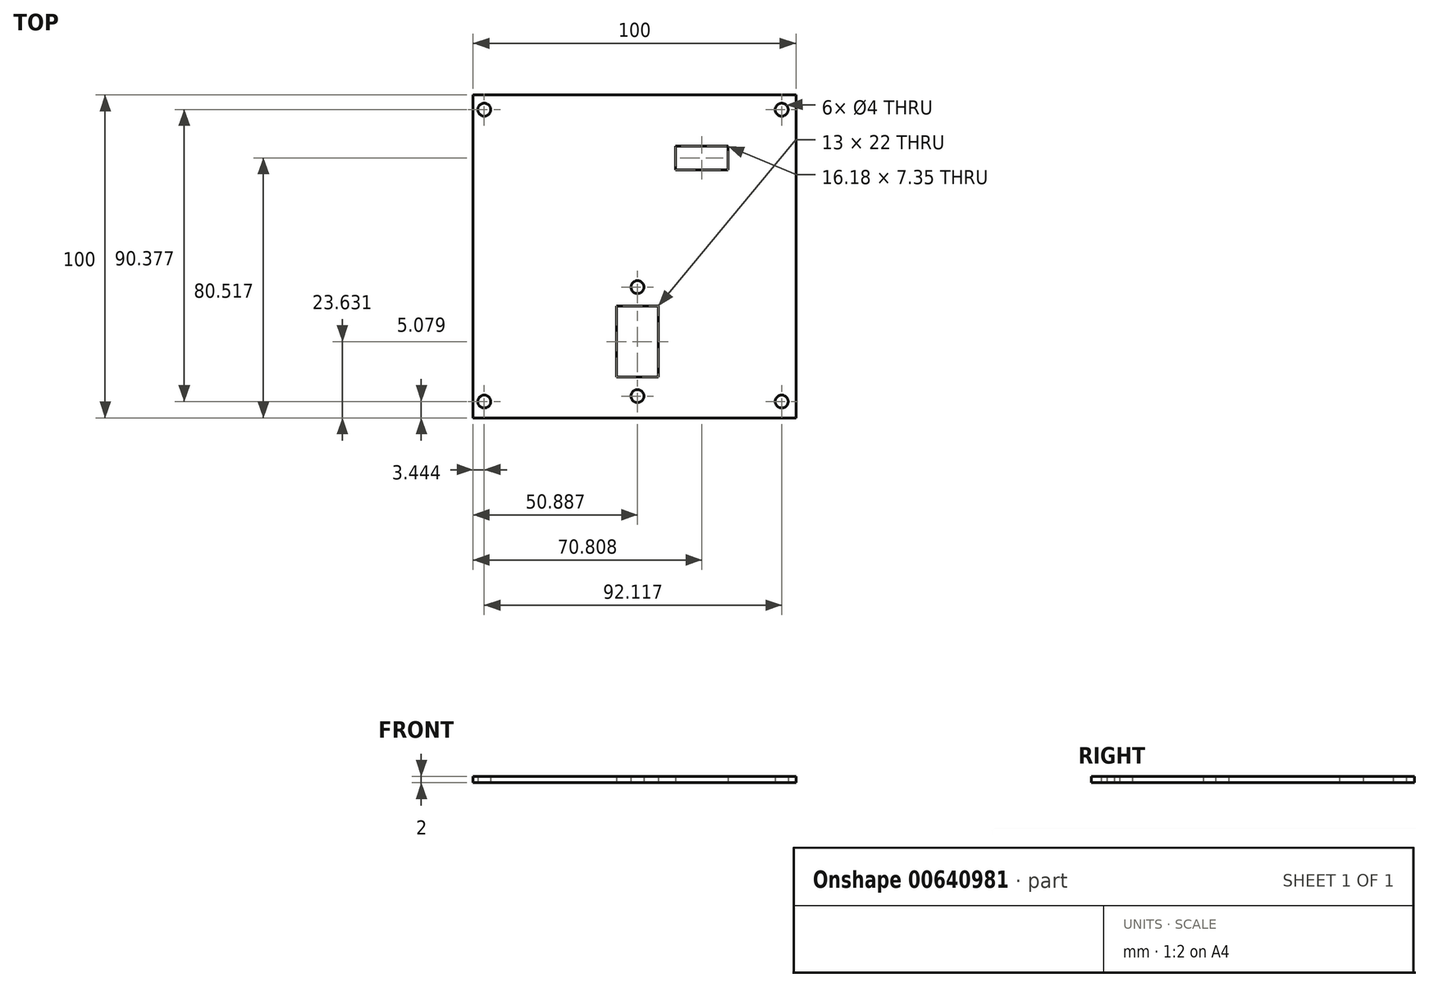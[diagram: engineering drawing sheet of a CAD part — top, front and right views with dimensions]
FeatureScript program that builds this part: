
annotation { "Feature Type Name" : "Feature", "Feature Type Description" : "" }
export const myFeature = defineFeature(function(context is Context, id is Id, definition is map)
    precondition{}
    {
        {
            var Q0;
            Q0=qCreatedBy(makeId("Top.planeOp"),FACE);
            var sketch = newSketch(context, id + "F0", { "sketchPlane" : qUnion([Q0])});
            skLineSegment(sketch, "E0.bottom", {"start": v(74.38, -40.51) * mm, "end": v(-25.62, -40.51) * mm});
            skLineSegment(sketch, "E0.top", {"start": v(74.38, 59.49) * mm, "end": v(-25.62, 59.49) * mm});
            skLineSegment(sketch, "E0.left", {"start": v(74.38, -40.51) * mm, "end": v(74.38, 59.49) * mm});
            skLineSegment(sketch, "E0.right", {"start": v(-25.62, -40.51) * mm, "end": v(-25.62, 59.49) * mm});
            skPoint(sketch, "E0.middle", {"position": v(21.05, 16.14) * mm});
            skPoint(sketch, "E1", {"position": v(-22.18, 54.95) * mm});
            skPoint(sketch, "E2.MirrorP", {"position": v(69.94, 54.95) * mm});
            skPoint(sketch, "E3", {"position": v(-22.18, -35.43) * mm});
            skPoint(sketch, "E4.MirrorP", {"position": v(69.94, -35.43) * mm});
            skLineSegment(sketch, "E5", {"start": v(-22.18, 54.95) * mm, "end": v(-22.18, -35.43) * mm, "construction": true});
            skLineSegment(sketch, "E6.bottom", {"start": v(37.1, 43.68) * mm, "end": v(53.28, 43.68) * mm});
            skLineSegment(sketch, "E6.top", {"start": v(37.1, 36.33) * mm, "end": v(53.28, 36.33) * mm});
            skLineSegment(sketch, "E6.left", {"start": v(37.1, 43.68) * mm, "end": v(37.1, 36.33) * mm});
            skLineSegment(sketch, "E6.right", {"start": v(53.28, 43.68) * mm, "end": v(53.28, 36.33) * mm});
            skLineSegment(sketch, "E7.bottom", {"start": v(31.77, -27.88) * mm, "end": v(18.77, -27.88) * mm});
            skLineSegment(sketch, "E7.top", {"start": v(31.77, -5.88) * mm, "end": v(18.77, -5.88) * mm});
            skLineSegment(sketch, "E7.left", {"start": v(31.77, -27.88) * mm, "end": v(31.77, -5.88) * mm});
            skLineSegment(sketch, "E7.right", {"start": v(18.77, -27.88) * mm, "end": v(18.77, -5.88) * mm});
            skPoint(sketch, "E7.middle", {"position": v(25.27, -16.88) * mm});
            skCircle(sketch, "E8", {"center": v(25.27, 0) * mm, "radius": 2 * mm});
            skPoint(sketch, "E9", {"position": v(25.27, -5.88) * mm});
            skLineSegment(sketch, "E10", {"start": v(-2.74, -16.88) * mm, "end": v(45.62, -16.88) * mm, "construction": true});
            skLineSegment(sketch, "E11", {"start": v(-22.18, 54.95) * mm, "end": v(69.94, -35.43) * mm, "construction": true});
            skLineSegment(sketch, "E12", {"start": v(69.94, 54.95) * mm, "end": v(-22.18, -35.43) * mm, "construction": true});
            skPoint(sketch, "E13", {"position": v(23.88, 9.76) * mm});
            skCircle(sketch, "E14.MirrorC", {"center": v(25.27, -33.76) * mm, "radius": 2 * mm});
            skSolve(sketch);
        }
        {
            var Q0;
            Q0 = qSketchRegion(id + "F0", true);
            extrude(context, id + "F1", {"entities" : qUnion([Q0]), "depth" : 2 * mm, "offsetDistance" : 25.4 * mm});
        }
        {
            var Q0;
            Q0=sQuery(id+"F0.wireOp",VERTEX,"E1");
            var Q1;
            Q1=sQuery(id+"F0.wireOp",VERTEX,"E4.MirrorP");
            var Q2;
            Q2=sQuery(id+"F0.wireOp",VERTEX,"E2.MirrorP");
            var Q3;
            Q3=sQuery(id+"F0.wireOp",VERTEX,"E3");
            var Q4;
            Q4=makeQuery(id+"F1.opExtrude","SWEPT_BODY",BODY,{"disambiguationData":[OSD([sQuery(id+"F0.wireOp",EDGE,"E0.bottom"),sQuery(id+"F0.wireOp",EDGE,"E0.top"),sQuery(id+"F0.wireOp",EDGE,"E0.left"),sQuery(id+"F0.wireOp",EDGE,"E0.right"),sQuery(id+"F0.wireOp",EDGE,"E6.bottom"),sQuery(id+"F0.wireOp",EDGE,"E6.top"),sQuery(id+"F0.wireOp",EDGE,"E6.left"),sQuery(id+"F0.wireOp",EDGE,"E6.right"),sQuery(id+"F0.wireOp",EDGE,"E7.bottom"),sQuery(id+"F0.wireOp",EDGE,"E7.top"),sQuery(id+"F0.wireOp",EDGE,"E7.left"),sQuery(id+"F0.wireOp",EDGE,"E7.right"),sQuery(id+"F0.wireOp",EDGE,"E8"),sQuery(id+"F0.wireOp",EDGE,"cb9998cb-29bc-4fc8-b8aa-ae402117172b0.MirrorC")])]});
            hole(context, id + "F2", {"style" : HoleStyle.SIMPLE, "endStyle" : HoleEndStyle.BLIND, "oppositeDirection" : true, "holeDiameter" : 4 * mm, "majorDiameter" : 6.35 * mm, "holeDepth" : 15 * mm, "isTappedThrough" : true, "tappedDepth" : 12.7 * mm, "tapClearance" : 3, "locations" : qUnion([Q0, Q1, Q2, Q3]), "scope" : qUnion([Q4])});
        }
    });
